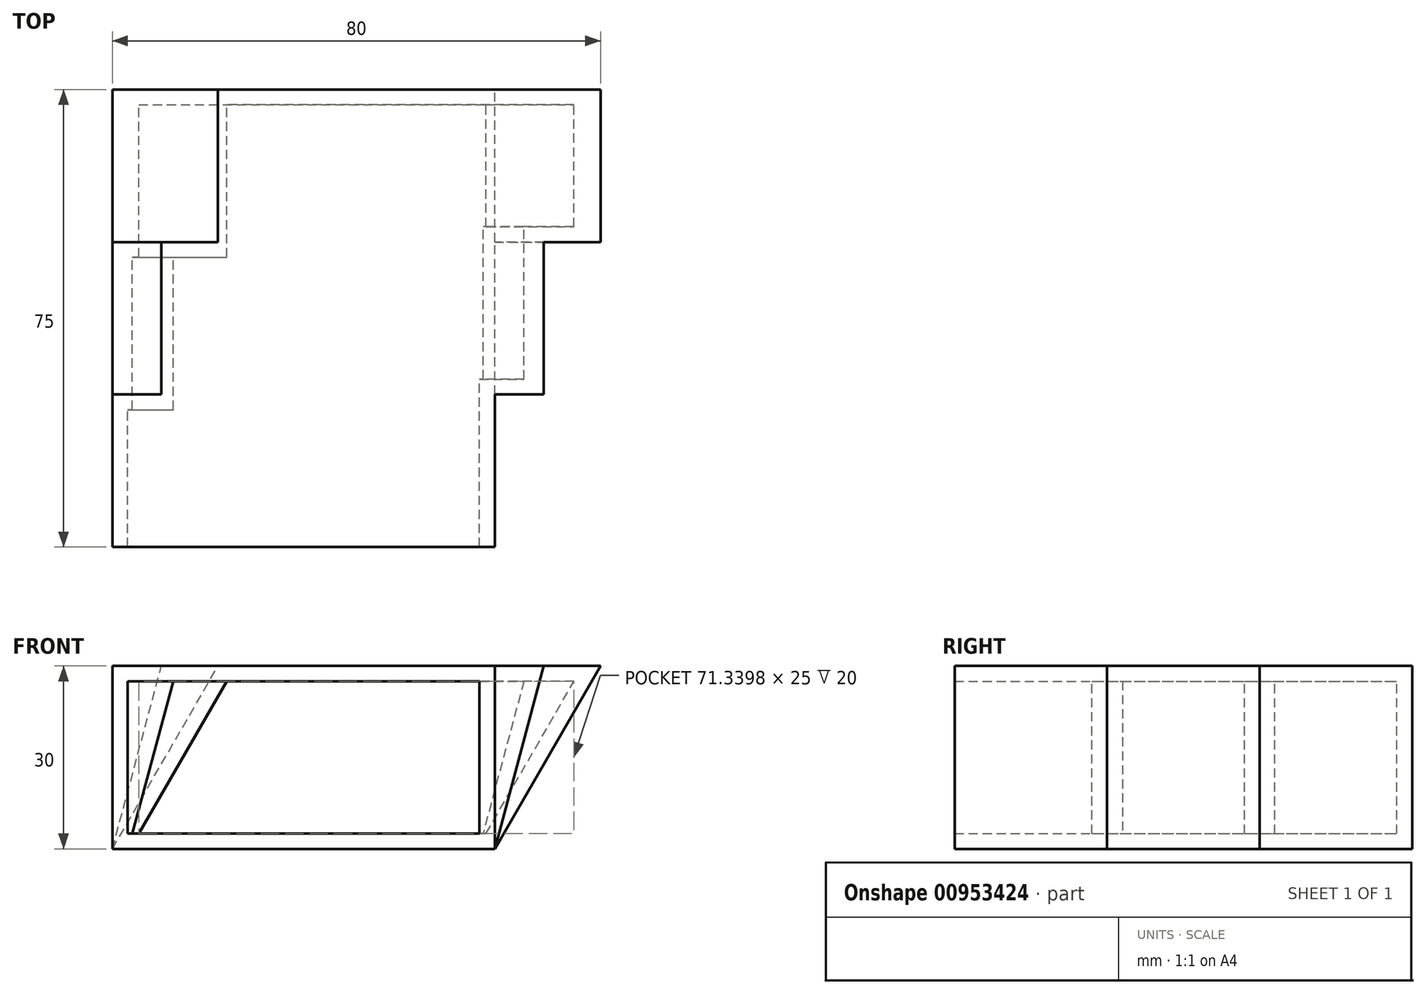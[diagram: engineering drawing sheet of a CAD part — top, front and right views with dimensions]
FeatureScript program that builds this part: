
annotation { "Feature Type Name" : "Feature", "Feature Type Description" : "" }
export const myFeature = defineFeature(function(context is Context, id is Id, definition is map)
    precondition{}
    {
        {
            var Q0;
            Q0=qCreatedBy(makeId("Front.planeOp"),FACE);
            var sketch = newSketch(context, id + "F0", { "sketchPlane" : qUnion([Q0])});
            skLineSegment(sketch, "E0", {"start": v(-40, 0) * mm, "end": v(-22.68, 30) * mm});
            skLineSegment(sketch, "E1", {"start": v(-40, 0) * mm, "end": v(22.68, 0) * mm});
            skLineSegment(sketch, "E2", {"start": v(22.68, 0) * mm, "end": v(40, 30) * mm});
            skLineSegment(sketch, "E3", {"start": v(40, 30) * mm, "end": v(-22.68, 30) * mm});
            skLineSegment(sketch, "E4", {"start": v(-31.34, 15) * mm, "end": v(31.34, 15) * mm, "construction": true});
            skSolve(sketch);
        }
        {
            var Q0;
            Q0 = qSketchRegion(id + "F0", true);
            extrude(context, id + "F1", {"entities" : qUnion([Q0]), "depth" : 25 * mm, "offsetDistance" : 25 * mm});
        }
        {
            var Q0;
            Q0=makeQuery(id+"F1.opExtrude","CAP_FACE",FACE,{"disambiguationData":[OSD([sQuery(id+"F0.wireOp",EDGE,"E0"),sQuery(id+"F0.wireOp",EDGE,"E1"),sQuery(id+"F0.wireOp",EDGE,"E2"),sQuery(id+"F0.wireOp",EDGE,"E3")])],"isStart":false});
            var sketch = newSketch(context, id + "F2", { "sketchPlane" : qUnion([Q0])});
            skLineSegment(sketch, "E5", {"start": v(-40, 0) * mm, "end": v(-31.96, 30) * mm});
            skLineSegment(sketch, "E6", {"start": v(-31.96, 30) * mm, "end": v(30.72, 30) * mm});
            skLineSegment(sketch, "E7", {"start": v(30.72, 30) * mm, "end": v(22.68, 0) * mm});
            skLineSegment(sketch, "E8", {"start": v(22.68, 0) * mm, "end": v(-40, 0) * mm});
            skSolve(sketch);
        }
        {
            var Q0;
            Q0 = qSketchRegion(id + "F2", true);
            extrude(context, id + "F3", {"entities" : qUnion([Q0]), "operationType" : NewBodyOperationType.ADD, "depth" : 25 * mm, "offsetDistance" : 25 * mm});
        }
        {
            var Q0;
            Q0=makeQuery(id+"F3.opExtrude","CAP_FACE",FACE,{"disambiguationData":[OSD([sQuery(id+"F2.wireOp",EDGE,"E5"),sQuery(id+"F2.wireOp",EDGE,"E6"),sQuery(id+"F2.wireOp",EDGE,"E7"),sQuery(id+"F2.wireOp",EDGE,"E8")])],"isStart":false});
            var sketch = newSketch(context, id + "F4", { "sketchPlane" : qUnion([Q0])});
            skLineSegment(sketch, "E9.bottom", {"start": v(-40, 0) * mm, "end": v(22.68, 0) * mm});
            skLineSegment(sketch, "E9.top", {"start": v(-40, 30) * mm, "end": v(22.68, 30) * mm});
            skLineSegment(sketch, "E9.left", {"start": v(-40, 0) * mm, "end": v(-40, 30) * mm});
            skLineSegment(sketch, "E9.right", {"start": v(22.68, 0) * mm, "end": v(22.68, 30) * mm});
            skSolve(sketch);
        }
        {
            var Q0;
            Q0 = qSketchRegion(id + "F4", true);
            extrude(context, id + "F5", {"entities" : qUnion([Q0]), "operationType" : NewBodyOperationType.ADD, "depth" : 25 * mm, "offsetDistance" : 25 * mm});
        }
        {
            var Q0;
            Q0=makeQuery(id+"F5.opExtrude","CAP_FACE",FACE,{"disambiguationData":[OSD([sQuery(id+"F4.wireOp",EDGE,"E9.bottom"),sQuery(id+"F4.wireOp",EDGE,"E9.top"),sQuery(id+"F4.wireOp",EDGE,"E9.left"),sQuery(id+"F4.wireOp",EDGE,"E9.right")])],"isStart":false});
            shell(context, id + "F6", {"entities" : qUnion([Q0]), "thickness" : 2.5 * mm});
        }
    });
